# Revit family: Sanitary_Basins_Johnson-Suisse_Egg_Junior_Basin
name_source: partatom
category: Plumbing Fixtures
revit_build: Autodesk Revit 2015 (Build: 20140606_1530(x64)
units: mm (PartAtom-declared; Revit-internal decimal feet)

## types (1)
- Egg Junior Basin
    BIMobject category = Basins
    Brand url = http://www.johnsonsuisse.com.au
    Design country = Thailand
    EAN code = https://8852425451866
    Edition number = 1
    IFC Classification = Sanitary Terminal
    Installation instructions = https://johnsonsuisse.com.au
    Manufacturer country = Thailand
    Manufacturer name = Johnson Suisse
    Material main = Vitreous china
    NBS Reference Code = 31-79
    NBS Reference Description = Sinks, Wash Basins And Troughs
    Nominal height = 350 mm  [stored 1.14829 ft]
    Nominal width = 510 mm  [stored 1.67323 ft]
    Product Guid = db9e370c-2420-436e-afbd-7021382ba00b
    Product SKU = C01427-1
    Product data url = https://bimobject.com
    Product family = Egg
    Product group = Basins
    Product url = https://johnsonsuisse.com.au
    QR code = http://bimobject.com
    Technical description = https://johnsonsuisse.com.au
    Type = egg_junior_basin : Default
    UNSPSC Code = 301815
    Uniclass 1.4 Code = L7212
    Uniclass 1.4 Description = Washbasins
    Uniclass 2.0 Code = PR-31-79
    Uniclass 2.0 Description = Sinks, Wash Basins And Troughs
    Uniclass 2015 Code = Pr_40_20_96
    Uniclass 2015 Name = Wash basins, sinks and troughs
    Weight Net (Kg) = 17.5

note: [stored X ft] marks values corroborated as IEEE doubles in the binary element streams (Revit-internal decimal feet)

## geometry (parser evidence)
native form markers: Sweep x5
no freeform markers — native parametric forms only
